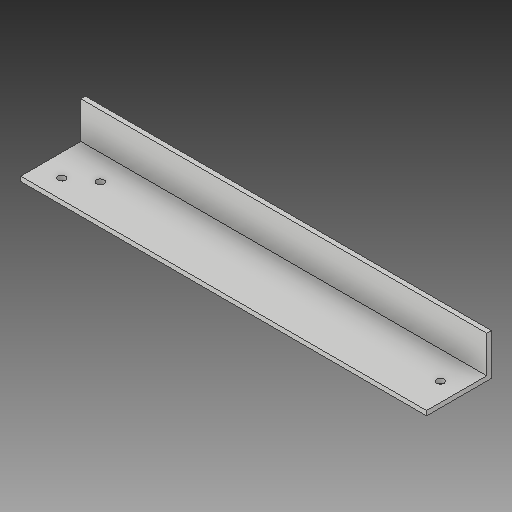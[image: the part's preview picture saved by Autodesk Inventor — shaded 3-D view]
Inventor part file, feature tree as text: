
AUTODESK INVENTOR PART (.ipt)
format: ipt  version: 2018 (Build 220112000, 112)  size: 112,128 bytes
history: native  units: in
note: dims shown in document units (in); Inventor stores cm internally (conversion verified against a paired STEP export)
features: sketch x4, other x3
ambient origin geometry x8: Origin, YZ Plane, XZ Plane, XY Plane, X Axis, Y Axis, Z Axis, Center Point
bodies: Solid1 (feature_tree)
feature tree (7):
  other  "angle iron with  holes 2.ipt"
  other  "Solid1::angle iron with  holes 2.ipt"
  other  "TaggingFeature1"
  sketch  "Sketch1"  dims[d0=0.3937in]
  sketch  "Sketch2"
  sketch  "Sketch3"
  sketch  "Sketch4"
